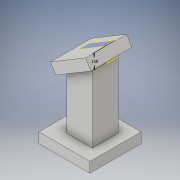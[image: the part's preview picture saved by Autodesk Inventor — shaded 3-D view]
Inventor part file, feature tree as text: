
AUTODESK INVENTOR PART (.ipt)
format: ipt  version: 2018 (Build 220112000, 112)  size: 140,288 bytes
history: native  units: in
note: dims shown in document units (in); Inventor stores cm internally (conversion verified against a paired STEP export)
features: sketch x5, extrude x4, plane x1, projected_geometry x1
ambient origin geometry x8: Origin, YZ Plane, XZ Plane, XY Plane, X Axis, Y Axis, Z Axis, Center Point
bodies: Solid1 (feature_tree)
feature tree (11):
  extrude  "Extrusion1"  Depth=0.5in
  extrude  "Extrusion2"  Depth=0.25in
  sketch  "Sketch3"  dims[d5=0.25in d6=0.125in]
  plane  "Work Plane1"
  extrude  "Extrusion3"  Depth=0.125in
  extrude  "Extrusion4"  Depth=0.1in TaperAngle=0.0deg
  sketch  "Sketch1"  dims[d0=0.5in d1=0.5in]
  sketch  "Sketch2"  dims[d2=0.1in d3=0.0in d4=0.25in]
  sketch  "Sketch4"  dims[d7=0.1in d8=0.65in d9=0.0in]
  sketch  "Sketch5"  dims[d10=0.15in d11=0.4in d12=0.4in d13=0.075in d14=0.1in d15=0.1in d16=0.0in d17=0.1in d18=0.0in]
  projected_geometry  "Projected Loop1"
